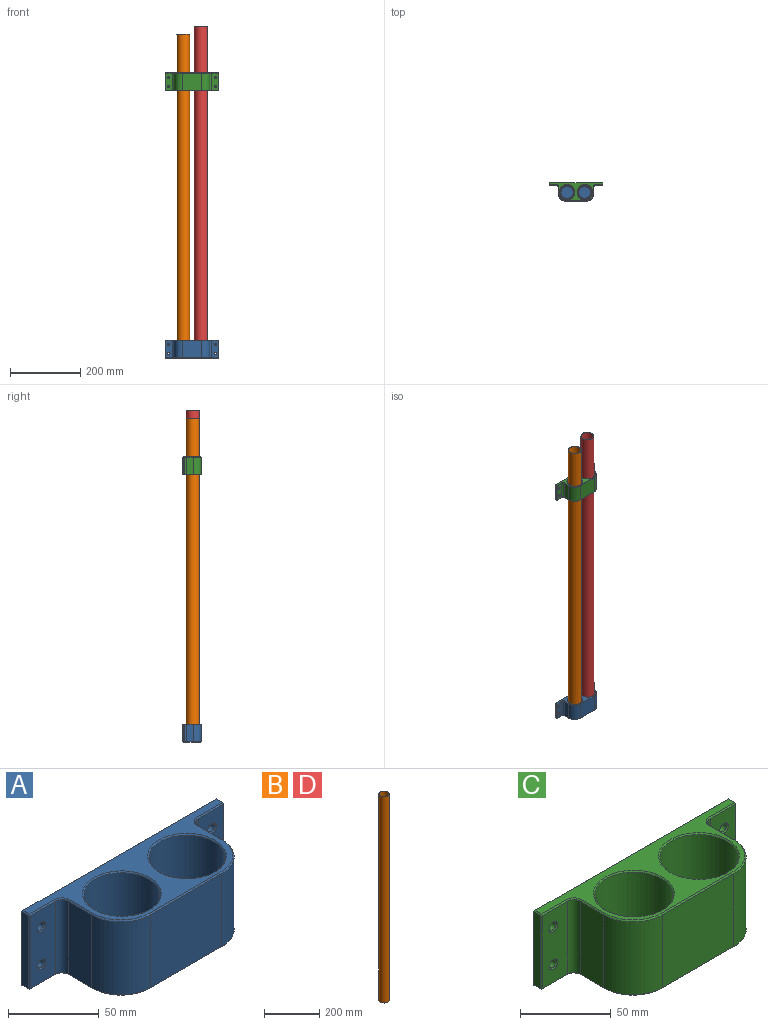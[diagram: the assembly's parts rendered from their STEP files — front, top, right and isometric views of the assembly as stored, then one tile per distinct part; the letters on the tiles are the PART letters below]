
ASSEMBLY  parts=4 mates=3
PART A: 70 faces, bbox 152.4x52.7x50.8 mm
  f0: plane 49.28x19.56mm, normal (0,-1,0), area 895.2mm2, adj f14,f38,f41,f42,f66,f67
  f1: plane 49.28x4.83mm, normal (-1,0,0), area 237.8mm2, adj f42,f47,f51,f52
  f2: plane 150.88x51.18mm, normal (0,0,-1), area 5172.2mm2, adj f28,f30,f31,f34,f35,f38,f39,f44
  f3: plane 49.28x4.83mm, normal (1,0,0), area 237.8mm2, adj f49,f58,f59,f63
  f4: cylinder r=2.54mm len=5.08mm, axis (0,1,0), area 77mm2, adj f25,f65
  f5: cylinder r=2.54mm len=5.08mm, axis (0,1,0), area 77mm2, adj f26,f66
  f6: cylinder r=2.54mm len=5.08mm, axis (0,1,0), area 77mm2, adj f27,f67
  f7: plane 150.88x51.18mm, normal (0,0,1), area 2208.9mm2, adj f29,f32,f33,f36,f37,f40,f41,f45
  f8: cylinder r=2.54mm len=5.08mm, axis (0,1,0), area 77mm2, adj f24,f64
  f9: plane 49.28x19.56mm, normal (0,-1,0), area 895.2mm2, adj f15,f48,f49,f50,f64,f65
  f10: plane 150.88x49.28mm, normal (0,1,0), area 7297.6mm2, adj f24,f25,f26,f27,f52,f57,f60,f63
  f11: plane 49.28x18.42mm, normal (-1,0,0), area 907.4mm2, adj f14,f20,f30,f33
  f12: plane 49.28x18.42mm, normal (1,0,0), area 907.4mm2, adj f15,f21,f39,f40
  f13: plane 55.88x49.28mm, normal (0,-1,0), area 2753.5mm2, adj f20,f21,f31,f32
  f14: cylinder r=5.08mm len=49.28mm, axis (0,0,1), area 393.2mm2, adj f0,f11,f34,f37
  f15: cylinder r=5.08mm len=49.28mm, axis (0,0,-1), area 393.2mm2, adj f9,f12,f44,f45
  f16: cylinder r=20.96mm len=42.93mm, axis (0,0,1), area 5651.8mm2, adj f22,f68
  f17: plane 40.39x40.39mm, normal (0,0,1), area 1281mm2, adj f22
  f18: cylinder r=20.96mm len=42.93mm, axis (0,0,1), area 5651.8mm2, adj f23,f69
  f19: plane 40.39x40.39mm, normal (0,0,1), area 1281mm2, adj f23
  f20: cylinder r=22.86mm len=49.28mm, axis (0,0,1), area 1769.4mm2, adj f11,f13,f28,f29
  f21: cylinder r=22.86mm len=49.28mm, axis (0,0,-1), area 1769.4mm2, adj f12,f13,f35,f36
  f22: cone r=20.19mm half-angle=45deg, axis (0,0,1), area 139.3mm2, adj f16,f17
  f23: cone r=20.19mm half-angle=45deg, axis (0,0,1), area 139.3mm2, adj f18,f19
  f24: cone r=3.3mm half-angle=45deg, axis (0,1,0), area 19.8mm2, adj f8,f10
  f25: cone r=3.3mm half-angle=45deg, axis (0,1,0), area 19.8mm2, adj f4,f10
  f26: cone r=3.3mm half-angle=45deg, axis (0,1,0), area 19.8mm2, adj f5,f10
  f27: cone r=3.3mm half-angle=45deg, axis (0,1,0), area 19.8mm2, adj f6,f10
  f28: cone r=22.1mm half-angle=45deg, axis (0,0,1), area 38.1mm2, adj f2,f20,f30,f31
  f29: cone r=22.1mm half-angle=45deg, axis (0,0,-1), area 38.1mm2, adj f7,f20,f32,f33
  f30: plane 18.42x0.76mm, normal (-0.71,0,-0.71), area 19.8mm2, adj f2,f11,f28,f34
  f31: plane 55.88x0.76mm, normal (0,-0.71,-0.71), area 60.2mm2, adj f2,f13,f28,f35
  f32: plane 55.88x0.76mm, normal (0,-0.71,0.71), area 60.2mm2, adj f7,f13,f29,f36
  f33: plane 18.42x0.76mm, normal (-0.71,0,0.71), area 19.8mm2, adj f7,f11,f29,f37
  f34: cone r=5.84mm half-angle=45deg, axis (0,0,-1), area 9.2mm2, adj f2,f14,f30,f38
  f35: cone r=22.1mm half-angle=45deg, axis (0,0,1), area 38.1mm2, adj f2,f21,f31,f39
  f36: cone r=22.1mm half-angle=45deg, axis (0,0,-1), area 38.1mm2, adj f7,f21,f32,f40
  f37: cone r=5.84mm half-angle=45deg, axis (0,0,1), area 9.2mm2, adj f7,f14,f33,f41
  f38: plane 19.56x0.76mm, normal (0,-0.71,-0.71), area 21.1mm2, adj f0,f2,f34,f43
  f39: plane 18.42x0.76mm, normal (0.71,0,-0.71), area 19.8mm2, adj f2,f12,f35,f44
  f40: plane 18.42x0.76mm, normal (0.71,0,0.71), area 19.8mm2, adj f7,f12,f36,f45
  f41: plane 19.56x0.76mm, normal (0,-0.71,0.71), area 21.1mm2, adj f0,f7,f37,f46
  f42: plane 49.28x0.76mm, normal (-0.71,-0.71,0), area 53.1mm2, adj f0,f1,f43,f46
  f43: plane 0.76x0.76mm, normal (-0.58,-0.58,-0.58), area 0.5mm2, adj f38,f42,f47
  f44: cone r=5.84mm half-angle=45deg, axis (0,0,-1), area 9.2mm2, adj f2,f15,f39,f48
  f45: cone r=5.84mm half-angle=45deg, axis (0,0,1), area 9.2mm2, adj f7,f15,f40,f50
  f46: plane 0.76x0.76mm, normal (-0.58,-0.58,0.58), area 0.5mm2, adj f41,f42,f51
  f47: plane 4.83x0.76mm, normal (-0.71,0,-0.71), area 5.2mm2, adj f1,f2,f43,f53
  f48: plane 19.56x0.76mm, normal (0,-0.71,-0.71), area 21.1mm2, adj f2,f9,f44,f54
  f49: plane 49.28x0.76mm, normal (0.71,-0.71,0), area 53.1mm2, adj f3,f9,f54,f55
  f50: plane 19.56x0.76mm, normal (0,-0.71,0.71), area 21.1mm2, adj f7,f9,f45,f55
  f51: plane 4.83x0.76mm, normal (-0.71,0,0.71), area 5.2mm2, adj f1,f7,f46,f56
  f52: plane 49.28x0.76mm, normal (-0.71,0.71,0), area 53.1mm2, adj f1,f10,f53,f56
  f53: plane 0.76x0.76mm, normal (-0.58,0.58,-0.58), area 0.5mm2, adj f47,f52,f57
  f54: plane 0.76x0.76mm, normal (0.58,-0.58,-0.58), area 0.5mm2, adj f48,f49,f58
  f55: plane 0.76x0.76mm, normal (0.58,-0.58,0.58), area 0.5mm2, adj f49,f50,f59
  f56: plane 0.76x0.76mm, normal (-0.58,0.58,0.58), area 0.5mm2, adj f51,f52,f60
  f57: plane 150.88x0.76mm, normal (0,0.71,-0.71), area 162.6mm2, adj f2,f10,f53,f61
  f58: plane 4.83x0.76mm, normal (0.71,0,-0.71), area 5.2mm2, adj f2,f3,f54,f61
  f59: plane 4.83x0.76mm, normal (0.71,0,0.71), area 5.2mm2, adj f3,f7,f55,f62
  f60: plane 150.88x0.76mm, normal (0,0.71,0.71), area 162.6mm2, adj f7,f10,f56,f62
  f61: plane 0.76x0.76mm, normal (0.58,0.58,-0.58), area 0.5mm2, adj f57,f58,f63
  f62: plane 0.76x0.76mm, normal (0.58,0.58,0.58), area 0.5mm2, adj f59,f60,f63
  f63: plane 49.28x0.76mm, normal (0.71,0.71,0), area 53.1mm2, adj f3,f10,f61,f62
  f64: cone r=2.54mm half-angle=45deg, axis (0,-1,0), area 19.8mm2, adj f8,f9
  f65: cone r=2.54mm half-angle=45deg, axis (0,-1,0), area 19.8mm2, adj f4,f9
  f66: cone r=2.54mm half-angle=45deg, axis (0,-1,0), area 19.8mm2, adj f0,f5
  f67: cone r=2.54mm half-angle=45deg, axis (0,-1,0), area 19.8mm2, adj f0,f6
  f68: cone r=20.96mm half-angle=45deg, axis (0,0,1), area 144.5mm2, adj f7,f16
  f69: cone r=20.96mm half-angle=45deg, axis (0,0,1), area 144.5mm2, adj f7,f18
PART B: 4 faces, bbox 36.8x36.8x914.4 mm
  f0: cylinder r=17.4mm len=914.4mm, axis (0,0,-1), area 99963.3mm2, adj f2,f3
  f1: cylinder r=18.41mm len=914.4mm, axis (0,0,-1), area 105800.5mm2, adj f2,f3
  f2: plane 36.83x36.83mm, normal (0,0,1), area 114.3mm2, adj f0,f1
  f3: plane 36.83x36.83mm, normal (0,0,-1), area 114.3mm2, adj f0,f1
PART C: 68 faces, bbox 152.4x52.7x50.8 mm
  f0: plane 49.28x19.56mm, normal (0,-1,0), area 895.2mm2, adj f14,f34,f37,f38,f64,f65
  f1: plane 49.28x4.83mm, normal (-1,0,0), area 237.8mm2, adj f38,f43,f47,f48
  f2: plane 150.88x51.18mm, normal (0,0,-1), area 2033.1mm2, adj f24,f26,f27,f30,f31,f34,f35,f40
  f3: plane 49.28x4.83mm, normal (1,0,0), area 237.8mm2, adj f45,f54,f55,f59
  f4: cylinder r=2.54mm len=5.08mm, axis (0,1,0), area 77mm2, adj f21,f63
  f5: cylinder r=2.54mm len=5.08mm, axis (0,1,0), area 77mm2, adj f22,f64
  f6: cylinder r=2.54mm len=5.08mm, axis (0,1,0), area 77mm2, adj f23,f65
  f7: plane 150.88x51.18mm, normal (0,0,1), area 2033.1mm2, adj f25,f28,f29,f32,f33,f36,f37,f41
  f8: cylinder r=2.54mm len=5.08mm, axis (0,1,0), area 77mm2, adj f20,f62
  f9: plane 49.28x19.56mm, normal (0,-1,0), area 895.2mm2, adj f15,f44,f45,f46,f62,f63
  f10: plane 150.88x49.28mm, normal (0,1,0), area 7297.6mm2, adj f20,f21,f22,f23,f48,f53,f56,f59
  f11: plane 49.28x18.42mm, normal (-1,0,0), area 907.4mm2, adj f14,f18,f26,f29
  f12: plane 49.28x18.42mm, normal (1,0,0), area 907.4mm2, adj f15,f19,f35,f36
  f13: plane 55.88x49.28mm, normal (0,-1,0), area 2753.5mm2, adj f18,f19,f27,f28
  f14: cylinder r=5.08mm len=49.28mm, axis (0,0,1), area 393.2mm2, adj f0,f11,f30,f33
  f15: cylinder r=5.08mm len=49.28mm, axis (0,0,-1), area 393.2mm2, adj f9,f12,f40,f41
  f16: cylinder r=21.59mm len=49.28mm, axis (0,0,1), area 6684.5mm2, adj f60,f66
  f17: cylinder r=21.59mm len=49.28mm, axis (0,0,1), area 6684.5mm2, adj f61,f67
  f18: cylinder r=22.86mm len=49.28mm, axis (0,0,1), area 1769.4mm2, adj f11,f13,f24,f25
  f19: cylinder r=22.86mm len=49.28mm, axis (0,0,-1), area 1769.4mm2, adj f12,f13,f31,f32
  f20: cone r=3.3mm half-angle=45deg, axis (0,1,0), area 19.8mm2, adj f8,f10
  f21: cone r=3.3mm half-angle=45deg, axis (0,1,0), area 19.8mm2, adj f4,f10
  f22: cone r=3.3mm half-angle=45deg, axis (0,1,0), area 19.8mm2, adj f5,f10
  f23: cone r=3.3mm half-angle=45deg, axis (0,1,0), area 19.8mm2, adj f6,f10
  f24: cone r=22.1mm half-angle=45deg, axis (0,0,1), area 38.1mm2, adj f2,f18,f26,f27
  f25: cone r=22.1mm half-angle=45deg, axis (0,0,-1), area 38.1mm2, adj f7,f18,f28,f29
  f26: plane 18.42x0.76mm, normal (-0.71,0,-0.71), area 19.8mm2, adj f2,f11,f24,f30
  f27: plane 55.88x0.76mm, normal (0,-0.71,-0.71), area 60.2mm2, adj f2,f13,f24,f31
  f28: plane 55.88x0.76mm, normal (0,-0.71,0.71), area 60.2mm2, adj f7,f13,f25,f32
  f29: plane 18.42x0.76mm, normal (-0.71,0,0.71), area 19.8mm2, adj f7,f11,f25,f33
  f30: cone r=5.84mm half-angle=45deg, axis (0,0,-1), area 9.2mm2, adj f2,f14,f26,f34
  f31: cone r=22.1mm half-angle=45deg, axis (0,0,1), area 38.1mm2, adj f2,f19,f27,f35
  f32: cone r=22.1mm half-angle=45deg, axis (0,0,-1), area 38.1mm2, adj f7,f19,f28,f36
  f33: cone r=5.84mm half-angle=45deg, axis (0,0,1), area 9.2mm2, adj f7,f14,f29,f37
  f34: plane 19.56x0.76mm, normal (0,-0.71,-0.71), area 21.1mm2, adj f0,f2,f30,f39
  f35: plane 18.42x0.76mm, normal (0.71,0,-0.71), area 19.8mm2, adj f2,f12,f31,f40
  f36: plane 18.42x0.76mm, normal (0.71,0,0.71), area 19.8mm2, adj f7,f12,f32,f41
  f37: plane 19.56x0.76mm, normal (0,-0.71,0.71), area 21.1mm2, adj f0,f7,f33,f42
  f38: plane 49.28x0.76mm, normal (-0.71,-0.71,0), area 53.1mm2, adj f0,f1,f39,f42
  f39: plane 0.76x0.76mm, normal (-0.58,-0.58,-0.58), area 0.5mm2, adj f34,f38,f43
  f40: cone r=5.84mm half-angle=45deg, axis (0,0,-1), area 9.2mm2, adj f2,f15,f35,f44
  f41: cone r=5.84mm half-angle=45deg, axis (0,0,1), area 9.2mm2, adj f7,f15,f36,f46
  f42: plane 0.76x0.76mm, normal (-0.58,-0.58,0.58), area 0.5mm2, adj f37,f38,f47
  f43: plane 4.83x0.76mm, normal (-0.71,0,-0.71), area 5.2mm2, adj f1,f2,f39,f49
  f44: plane 19.56x0.76mm, normal (0,-0.71,-0.71), area 21.1mm2, adj f2,f9,f40,f50
  f45: plane 49.28x0.76mm, normal (0.71,-0.71,0), area 53.1mm2, adj f3,f9,f50,f51
  f46: plane 19.56x0.76mm, normal (0,-0.71,0.71), area 21.1mm2, adj f7,f9,f41,f51
  f47: plane 4.83x0.76mm, normal (-0.71,0,0.71), area 5.2mm2, adj f1,f7,f42,f52
  f48: plane 49.28x0.76mm, normal (-0.71,0.71,0), area 53.1mm2, adj f1,f10,f49,f52
  f49: plane 0.76x0.76mm, normal (-0.58,0.58,-0.58), area 0.5mm2, adj f43,f48,f53
  f50: plane 0.76x0.76mm, normal (0.58,-0.58,-0.58), area 0.5mm2, adj f44,f45,f54
  f51: plane 0.76x0.76mm, normal (0.58,-0.58,0.58), area 0.5mm2, adj f45,f46,f55
  f52: plane 0.76x0.76mm, normal (-0.58,0.58,0.58), area 0.5mm2, adj f47,f48,f56
  f53: plane 150.88x0.76mm, normal (0,0.71,-0.71), area 162.6mm2, adj f2,f10,f49,f57
  f54: plane 4.83x0.76mm, normal (0.71,0,-0.71), area 5.2mm2, adj f2,f3,f50,f57
  f55: plane 4.83x0.76mm, normal (0.71,0,0.71), area 5.2mm2, adj f3,f7,f51,f58
  f56: plane 150.88x0.76mm, normal (0,0.71,0.71), area 162.6mm2, adj f7,f10,f52,f58
  f57: plane 0.76x0.76mm, normal (0.58,0.58,-0.58), area 0.5mm2, adj f53,f54,f59
  f58: plane 0.76x0.76mm, normal (0.58,0.58,0.58), area 0.5mm2, adj f55,f56,f59
  f59: plane 49.28x0.76mm, normal (0.71,0.71,0), area 53.1mm2, adj f3,f10,f57,f58
  f60: cone r=22.35mm half-angle=45deg, axis (0,0,-1), area 148.8mm2, adj f2,f16
  f61: cone r=22.35mm half-angle=45deg, axis (0,0,-1), area 148.8mm2, adj f2,f17
  f62: cone r=2.54mm half-angle=45deg, axis (0,-1,0), area 19.8mm2, adj f8,f9
  f63: cone r=2.54mm half-angle=45deg, axis (0,-1,0), area 19.8mm2, adj f4,f9
  f64: cone r=2.54mm half-angle=45deg, axis (0,-1,0), area 19.8mm2, adj f0,f5
  f65: cone r=2.54mm half-angle=45deg, axis (0,-1,0), area 19.8mm2, adj f0,f6
  f66: cone r=21.59mm half-angle=45deg, axis (0,0,1), area 148.8mm2, adj f7,f16
  f67: cone r=21.59mm half-angle=45deg, axis (0,0,1), area 148.8mm2, adj f7,f17
PART D: same geometry as B
PLACE A t=(-52.3,32.19,-37.34)mm fixed
PLACE B t=(-1.5,4.25,-28.58)mm
PLACE C t=(-52.3,32.19,724.66)mm
PLACE D t=(49.3,4.25,-5.48)mm
MATE slider B.f0 <-> A.f18  axis (0,0,-1) through (-1.5,4.25,-28.58)mm
MATE planar A.f10 <-> C.f10  axis (0,1,0) through (23.9,32.19,-11.94)mm
MATE slider D.f1 <-> A.f16  axis (0,0,-1) through (49.3,4.25,-5.48)mm
